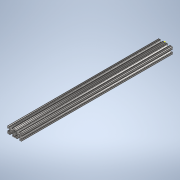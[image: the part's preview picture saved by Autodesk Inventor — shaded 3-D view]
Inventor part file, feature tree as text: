
AUTODESK INVENTOR PART (.ipt)
format: ipt  version: 2020 (Build 240168000, 168)  size: 352,768 bytes
history: native  units: in
note: dims shown in document units (in); Inventor stores cm internally (conversion verified against a paired STEP export)
features: sketch x2, extrude x1
ambient origin geometry x8: Origin, YZ Plane, XZ Plane, XY Plane, X Axis, Y Axis, Z Axis, Center Point
bodies: Solid1 (feature_tree)
feature tree (3):
  extrude  "Extrusion1"  [1 undecoded]
  sketch  "Sketch2"
  sketch  "Sketch1"  dims[d0=21.0in d1=0.0in]
note: 1 required parameter value undecoded (feature->parameter linkage not recoverable at this tier; creation-order binding heuristic only, values carry confidence <= 0.55)
